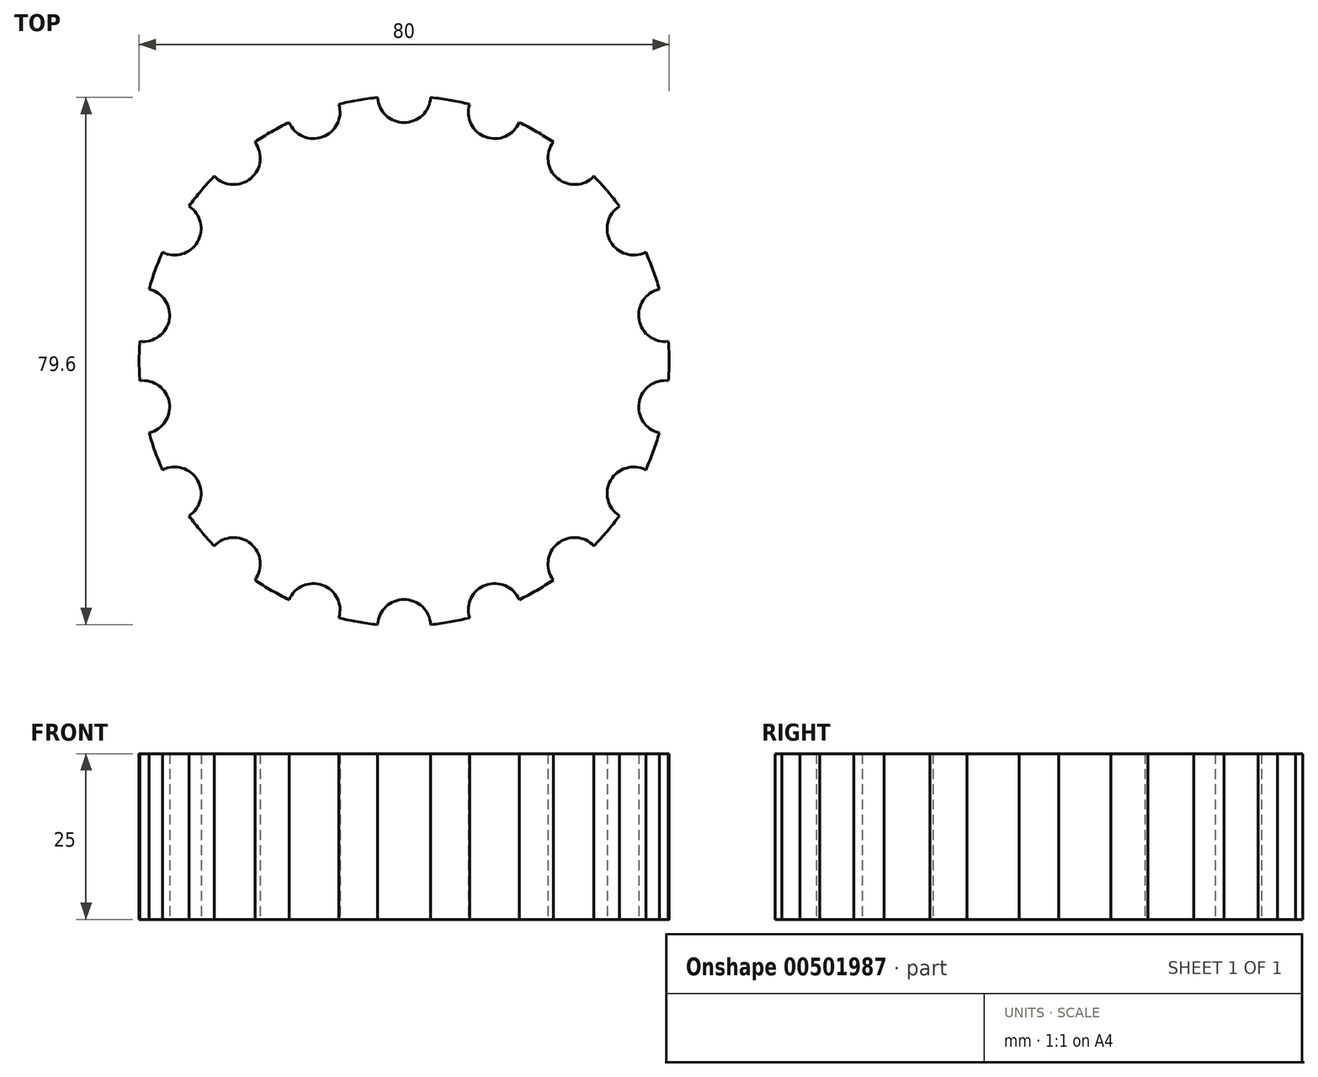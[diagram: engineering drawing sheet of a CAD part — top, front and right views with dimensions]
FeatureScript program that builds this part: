
annotation { "Feature Type Name" : "Feature", "Feature Type Description" : "" }
export const myFeature = defineFeature(function(context is Context, id is Id, definition is map)
    precondition{}
    {
        {
            var Q0;
            Q0=qCreatedBy(makeId("Top.planeOp"),FACE);
            var sketch = newSketch(context, id + "F0", { "sketchPlane" : qUnion([Q0])});
            skCircle(sketch, "E0", {"center": v(0, 0) * mm, "radius": 40 * mm});
            skArc(sketch, "E1", {"start": v(-4, 39.8) * mm, "mid": v(0, 36) * mm, "end": v(4, 39.8) * mm});
            skArc(sketch, "E2.1.0", {"start": v(-17.37, 36.03) * mm, "mid": v(-12.31, 33.83) * mm, "end": v(-9.86, 38.77) * mm});
            skArc(sketch, "E2.2.0", {"start": v(-28.64, 27.92) * mm, "mid": v(-23.14, 27.58) * mm, "end": v(-22.52, 33.06) * mm});
            skArc(sketch, "E2.3.0", {"start": v(-36.47, 16.44) * mm, "mid": v(-31.18, 18) * mm, "end": v(-32.47, 23.36) * mm});
            skArc(sketch, "E2.4.0", {"start": v(-39.89, 2.98) * mm, "mid": v(-35.45, 6.25) * mm, "end": v(-38.5, 10.85) * mm});
            skArc(sketch, "E2.5.0", {"start": v(-38.5, -10.85) * mm, "mid": v(-35.45, -6.25) * mm, "end": v(-39.89, -2.98) * mm});
            skArc(sketch, "E2.6.0", {"start": v(-32.47, -23.36) * mm, "mid": v(-31.18, -18) * mm, "end": v(-36.47, -16.44) * mm});
            skArc(sketch, "E2.7.0", {"start": v(-22.52, -33.06) * mm, "mid": v(-23.14, -27.58) * mm, "end": v(-28.64, -27.92) * mm});
            skArc(sketch, "E2.8.0", {"start": v(-9.86, -38.77) * mm, "mid": v(-12.31, -33.83) * mm, "end": v(-17.37, -36.03) * mm});
            skArc(sketch, "E2.9.0", {"start": v(4, -39.8) * mm, "mid": v(0, -36) * mm, "end": v(-4, -39.8) * mm});
            skArc(sketch, "E2.10.0", {"start": v(17.37, -36.03) * mm, "mid": v(12.31, -33.83) * mm, "end": v(9.86, -38.77) * mm});
            skArc(sketch, "E2.11.0", {"start": v(28.64, -27.92) * mm, "mid": v(23.14, -27.58) * mm, "end": v(22.52, -33.06) * mm});
            skArc(sketch, "E2.12.0", {"start": v(36.47, -16.44) * mm, "mid": v(31.18, -18) * mm, "end": v(32.47, -23.36) * mm});
            skArc(sketch, "E2.13.0", {"start": v(39.89, -2.98) * mm, "mid": v(35.45, -6.25) * mm, "end": v(38.5, -10.85) * mm});
            skArc(sketch, "E2.14.0", {"start": v(38.5, 10.85) * mm, "mid": v(35.45, 6.25) * mm, "end": v(39.89, 2.98) * mm});
            skArc(sketch, "E2.15.0", {"start": v(32.47, 23.36) * mm, "mid": v(31.18, 18) * mm, "end": v(36.47, 16.44) * mm});
            skArc(sketch, "E2.15.1", {"start": v(-4, 39.8) * mm, "mid": v(-29.32, -27.21) * mm, "end": v(39.4, -6.95) * mm});
            skArc(sketch, "E2.16.0", {"start": v(22.52, 33.06) * mm, "mid": v(23.14, 27.58) * mm, "end": v(28.64, 27.92) * mm});
            skArc(sketch, "E2.17.0", {"start": v(9.86, 38.77) * mm, "mid": v(12.31, 33.83) * mm, "end": v(17.37, 36.03) * mm});
            skArc(sketch, "E3.trimOffspring", {"start": v(39.89, -2.98) * mm, "mid": v(30.64, 25.71) * mm, "end": v(4, 39.8) * mm});
            skSolve(sketch);
        }
        {
            var Q0;
            {var subQ12=sQuery(id+"F0.wireOp",EDGE,"E1");Q0=makeQuery(id+"F0.imprint","IMPRINT",FACE,{"disambiguationData":[TD([[makeQuery(id+"F0.imprint","IMPRINT",EDGE,{"derivedFrom":subQ12}),-1.0]])]});}
            extrude(context, id + "F1", {"entities" : qUnion([Q0]), "endBound" : BoundingType.SYMMETRIC, "depth" : 25 * mm});
        }
    });
